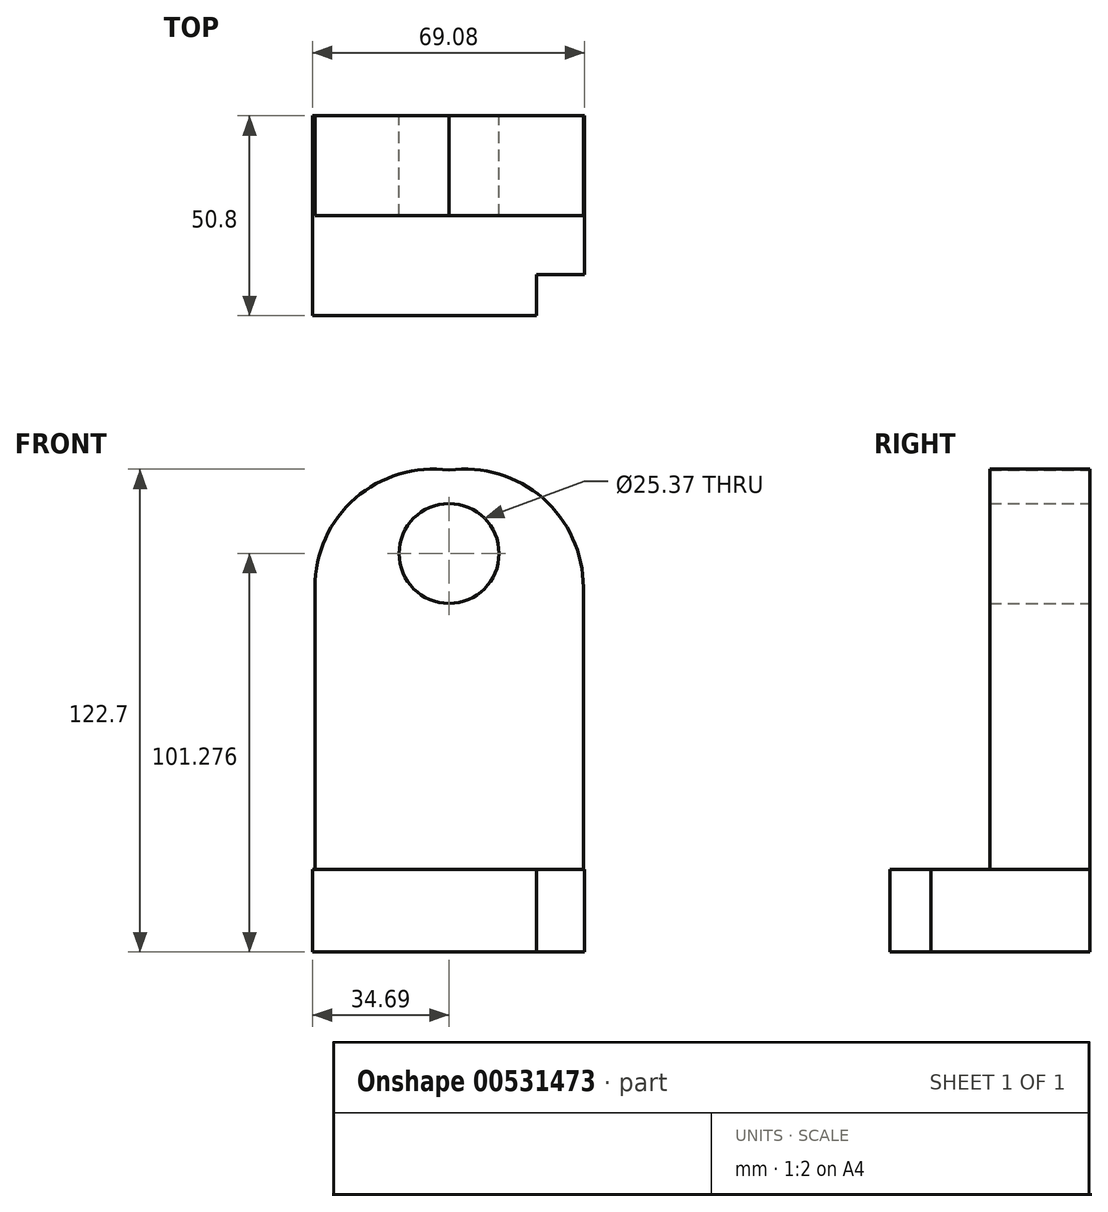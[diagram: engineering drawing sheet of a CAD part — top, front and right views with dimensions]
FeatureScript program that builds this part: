
annotation { "Feature Type Name" : "Feature", "Feature Type Description" : "" }
export const myFeature = defineFeature(function(context is Context, id is Id, definition is map)
    precondition{}
    {
        {
            var Q0;
            Q0=qCreatedBy(makeId("Front.planeOp"),FACE);
            var sketch = newSketch(context, id + "F0", { "sketchPlane" : qUnion([Q0])});
            skLineSegment(sketch, "E0.bottom", {"start": v(-34.1, 46.2) * mm, "end": v(34.1, 46.2) * mm});
            skLineSegment(sketch, "E0.top", {"start": v(-34.1, -46.2) * mm, "end": v(34.1, -46.2) * mm});
            skLineSegment(sketch, "E0.left", {"start": v(-34.1, 46.2) * mm, "end": v(-34.1, -46.2) * mm});
            skLineSegment(sketch, "E0.right", {"start": v(34.1, 46.2) * mm, "end": v(34.1, -46.2) * mm});
            skPoint(sketch, "E0.middle", {"position": v(0, 0) * mm});
            skArc(sketch, "E1", {"start": v(0, 75.93) * mm, "mid": v(-23.81, 68.82) * mm, "end": v(-34.1, 46.2) * mm});
            skArc(sketch, "E2", {"start": v(34.1, 46.2) * mm, "mid": v(23.81, 68.82) * mm, "end": v(0, 75.93) * mm});
            skSolve(sketch);
        }
        {
            var Q0;
            Q0=makeQuery(id+"F0.imprint","IMPRINT",FACE,{"disambiguationData":[TD([[makeQuery(id+"F0.imprint","IMPRINT",EDGE,{"derivedFrom":sQuery(id+"F0.wireOp",EDGE,"E0.bottom")}),1.0]])]});
            var Q1;
            Q1=makeQuery(id+"F0.imprint","IMPRINT",FACE,{"disambiguationData":[TD([[makeQuery(id+"F0.imprint","IMPRINT",EDGE,{"derivedFrom":sQuery(id+"F0.wireOp",EDGE,"E0.bottom")}),-1.0]])]});
            extrude(context, id + "F1", {"entities" : qUnion([Q0, Q1]), "depth" : 25.4 * mm, "offsetDistance" : 25.4 * mm});
        }
        {
            var Q0;
            Q0=qCreatedBy(makeId("Front.planeOp"),FACE);
            var sketch = newSketch(context, id + "F2", { "sketchPlane" : qUnion([Q0])});
            skCircle(sketch, "E3", {"center": v(0, 54.79) * mm, "radius": 12.68 * mm});
            skSolve(sketch);
        }
        {
            var Q0;
            Q0 = qSketchRegion(id + "F2", true);
            extrude(context, id + "F3", {"entities" : qUnion([Q0]), "operationType" : NewBodyOperationType.REMOVE, "endBound" : BoundingType.THROUGH_ALL, "depth" : 25.4 * mm, "offsetDistance" : 25.4 * mm});
        }
        {
            var Q0;
            Q0=qCreatedBy(makeId("Front.planeOp"),FACE);
            var sketch = newSketch(context, id + "F4", { "sketchPlane" : qUnion([Q0])});
            skLineSegment(sketch, "E4.bottom", {"start": v(-34.69, -46.5) * mm, "end": v(34.4, -46.5) * mm});
            skLineSegment(sketch, "E4.top", {"start": v(-34.69, -25.5) * mm, "end": v(34.4, -25.5) * mm});
            skLineSegment(sketch, "E4.left", {"start": v(-34.69, -46.5) * mm, "end": v(-34.69, -25.5) * mm});
            skLineSegment(sketch, "E4.right", {"start": v(34.4, -46.5) * mm, "end": v(34.4, -25.5) * mm});
            skSolve(sketch);
        }
        {
            var Q0;
            Q0 = qSketchRegion(id + "F4", true);
            var Q1;
            Q1=makeQuery(id+"F4.imprint","IMPRINT",FACE,{"disambiguationData":[TD([[makeQuery(id+"F4.imprint","IMPRINT",EDGE,{"derivedFrom":sQuery(id+"F4.wireOp",EDGE,"E4.bottom")}),1.0]])]});
            extrude(context, id + "F5", {"entities" : qUnion([Q0, Q1]), "operationType" : NewBodyOperationType.ADD, "depth" : 50.8 * mm, "offsetDistance" : 25.4 * mm});
        }
        {
            var Q0;
            Q0=qCreatedBy(makeId("Top.planeOp"),FACE);
            var sketch = newSketch(context, id + "F6", { "sketchPlane" : qUnion([Q0])});
            skLineSegment(sketch, "E5.bottom", {"start": v(39.64, -53.78) * mm, "end": v(22.15, -53.78) * mm});
            skLineSegment(sketch, "E5.top", {"start": v(39.64, -40.37) * mm, "end": v(22.15, -40.37) * mm});
            skLineSegment(sketch, "E5.left", {"start": v(39.64, -53.78) * mm, "end": v(39.64, -40.37) * mm});
            skLineSegment(sketch, "E5.right", {"start": v(22.15, -53.78) * mm, "end": v(22.15, -40.37) * mm});
            skSolve(sketch);
        }
        {
            var Q0;
            Q0 = qSketchRegion(id + "F6", true);
            extrude(context, id + "F7", {"entities" : qUnion([Q0]), "operationType" : NewBodyOperationType.REMOVE, "endBound" : BoundingType.THROUGH_ALL, "oppositeDirection" : true, "depth" : 25.4 * mm, "offsetDistance" : 25.4 * mm});
        }
    });
